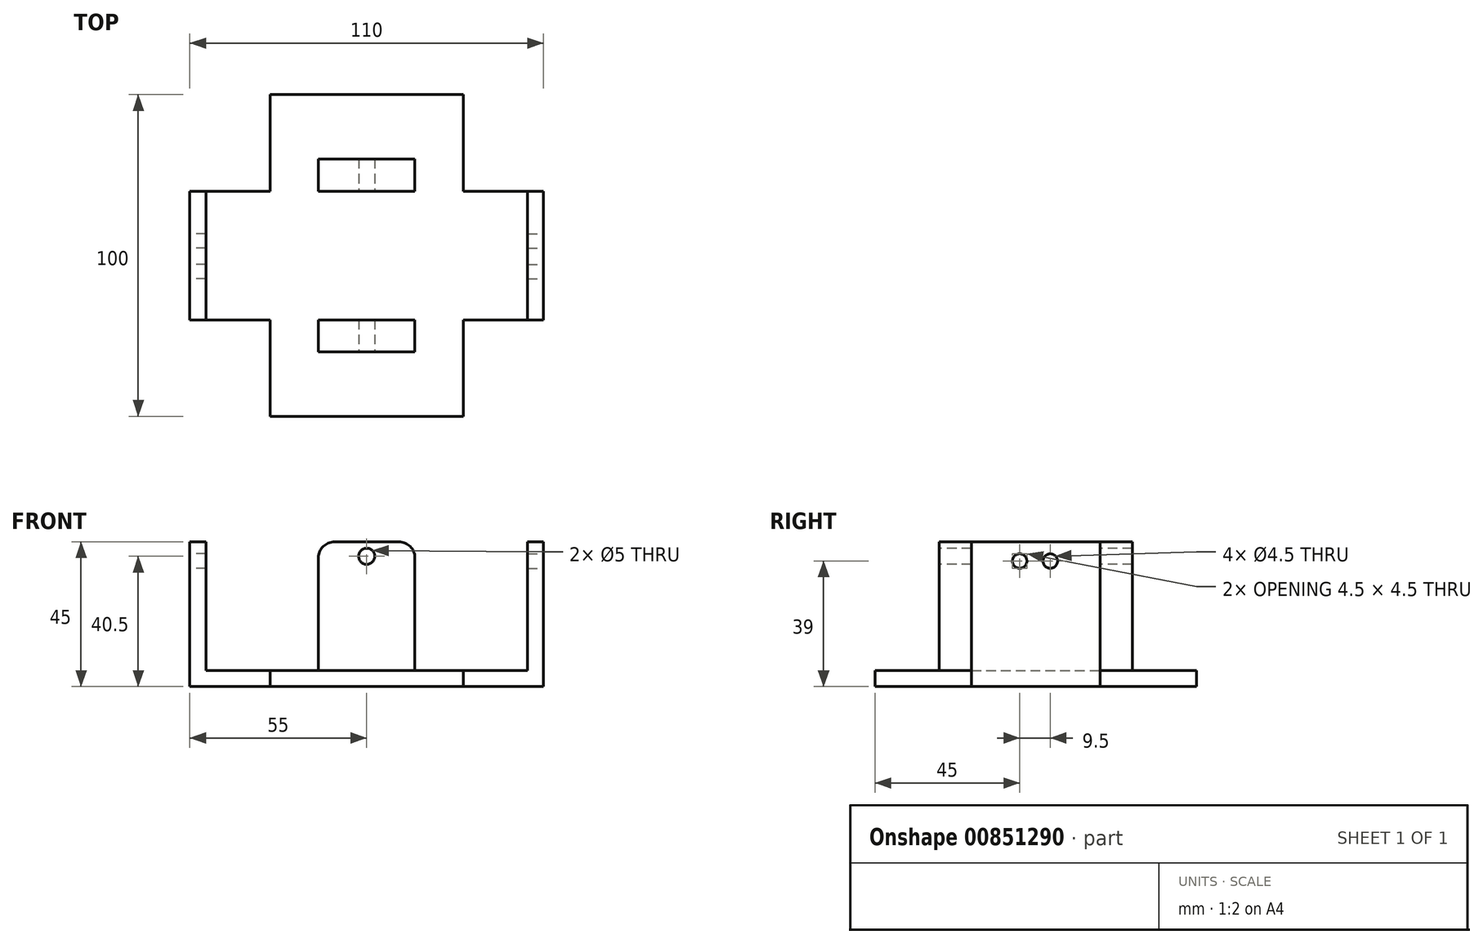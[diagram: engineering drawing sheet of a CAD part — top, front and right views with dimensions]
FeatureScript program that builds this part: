
annotation { "Feature Type Name" : "Feature", "Feature Type Description" : "" }
export const myFeature = defineFeature(function(context is Context, id is Id, definition is map)
    precondition{}
    {
        {
            var Q0;
            Q0=qCreatedBy(makeId("Top.planeOp"),FACE);
            var sketch = newSketch(context, id + "F0", { "sketchPlane" : qUnion([Q0])});
            skLineSegment(sketch, "E0.bottom", {"start": v(-30, -50) * mm, "end": v(30, -50) * mm});
            skLineSegment(sketch, "E0.top", {"start": v(-30, 50) * mm, "end": v(30, 50) * mm});
            skLineSegment(sketch, "E0.left", {"start": v(-30, -50) * mm, "end": v(-30, 50) * mm});
            skLineSegment(sketch, "E0.right", {"start": v(30, -50) * mm, "end": v(30, 50) * mm});
            skLineSegment(sketch, "E1", {"start": v(0, 50) * mm, "end": v(0, -50) * mm});
            skSolve(sketch);
        }
        {
            var Q0;
            {var subQ0=sQuery(id+"F0.wireOp",EDGE,"E0.left");Q0=makeQuery(id+"F0.imprint","IMPRINT",FACE,{"disambiguationData":[TD([[makeQuery(id+"F0.imprint","IMPRINT",EDGE,{"derivedFrom":subQ0}),-1.0]])]});}
            var Q1;
            {var subQ0=sQuery(id+"F0.wireOp",EDGE,"E0.right");Q1=makeQuery(id+"F0.imprint","IMPRINT",FACE,{"disambiguationData":[TD([[makeQuery(id+"F0.imprint","IMPRINT",EDGE,{"derivedFrom":subQ0}),1.0]])]});}
            extrude(context, id + "F1", {"entities" : qUnion([Q0, Q1]), "depth" : 5 * mm, "offsetDistance" : 25 * mm});
        }
        {
            var Q0;
            Q0=makeQuery(id+"F1.opExtrude","CAP_FACE",FACE,{"disambiguationData":[OSD([sQuery(id+"F0.wireOp",EDGE,"E0.bottom"),sQuery(id+"F0.wireOp",EDGE,"E0.top"),sQuery(id+"F0.wireOp",EDGE,"E0.left"),sQuery(id+"F0.wireOp",EDGE,"E0.right")])],"isStart":false});
            var sketch = newSketch(context, id + "F2", { "sketchPlane" : qUnion([Q0])});
            skLineSegment(sketch, "E2.bottom", {"start": v(-15, -20) * mm, "end": v(15, -20) * mm});
            skLineSegment(sketch, "E2.top", {"start": v(-15, -30) * mm, "end": v(15, -30) * mm});
            skLineSegment(sketch, "E2.left", {"start": v(-15, -20) * mm, "end": v(-15, -30) * mm});
            skLineSegment(sketch, "E2.right", {"start": v(15, -20) * mm, "end": v(15, -30) * mm});
            skLineSegment(sketch, "E3", {"start": v(-30, 0) * mm, "end": v(30, 0) * mm});
            skLineSegment(sketch, "E4.MirrorCS", {"start": v(-15, 20) * mm, "end": v(15, 20) * mm});
            skLineSegment(sketch, "E5.MirrorCS", {"start": v(15, 20) * mm, "end": v(15, 30) * mm});
            skLineSegment(sketch, "E6.MirrorCS", {"start": v(-15, 30) * mm, "end": v(15, 30) * mm});
            skLineSegment(sketch, "E7.MirrorCS", {"start": v(-15, 20) * mm, "end": v(-15, 30) * mm});
            skSolve(sketch);
        }
        {
            var Q0;
            Q0=makeQuery(id+"F2.imprint","IMPRINT",FACE,{"disambiguationData":[TD([[makeQuery(id+"F2.imprint","IMPRINT",EDGE,{"derivedFrom":sQuery(id+"F2.wireOp",EDGE,"E4.MirrorCS")}),1.0]])]});
            var Q1;
            Q1=makeQuery(id+"F2.imprint","IMPRINT",FACE,{"disambiguationData":[TD([[makeQuery(id+"F2.imprint","IMPRINT",EDGE,{"derivedFrom":sQuery(id+"F2.wireOp",EDGE,"E2.bottom")}),-1.0]])]});
            extrude(context, id + "F3", {"entities" : qUnion([Q0, Q1]), "operationType" : NewBodyOperationType.ADD, "depth" : 40 * mm, "offsetDistance" : 25 * mm});
        }
        {
            var Q0;
            Q0=makeQuery(id+"F3.opExtrude","CAP_EDGE",EDGE,{"disambiguationData":[OSD([sQuery(id+"F2.wireOp",EDGE,"E2.left")])],"isStart":false});
            var Q1;
            Q1=makeQuery(id+"F3.opExtrude","CAP_EDGE",EDGE,{"disambiguationData":[OSD([sQuery(id+"F2.wireOp",EDGE,"E2.right")])],"isStart":false});
            var Q2;
            Q2=makeQuery(id+"F3.opExtrude","CAP_EDGE",EDGE,{"disambiguationData":[OSD([sQuery(id+"F2.wireOp",EDGE,"E7.MirrorCS")])],"isStart":false});
            var Q3;
            Q3=makeQuery(id+"F3.opExtrude","CAP_EDGE",EDGE,{"disambiguationData":[OSD([sQuery(id+"F2.wireOp",EDGE,"E5.MirrorCS")])],"isStart":false});
            fillet(context, id + "F4", {"entities" : qUnion([Q0, Q1, Q2, Q3]), "radius" : 5 * mm, "tangentPropagation" : true, "allowEdgeOverflow" : false});
        }
        {
            var Q0;
            Q0=makeQuery(id+"F3.opExtrude","SWEPT_FACE",FACE,{"disambiguationData":[OSD([sQuery(id+"F2.wireOp",EDGE,"E2.top")])]});
            var sketch = newSketch(context, id + "F5", { "sketchPlane" : qUnion([Q0])});
            skCircle(sketch, "E8", {"center": v(0, 40.5) * mm, "radius": 2.5 * mm});
            skSolve(sketch);
        }
        {
            var Q0;
            Q0=makeQuery(id+"F5.imprint","IMPRINT",FACE,{"disambiguationData":[TD([[makeQuery(id+"F5.imprint","IMPRINT",EDGE,{"derivedFrom":sQuery(id+"F5.wireOp",EDGE,"E8")}),1.0]])]});
            extrude(context, id + "F6", {"entities" : qUnion([Q0]), "operationType" : NewBodyOperationType.REMOVE, "endBound" : BoundingType.THROUGH_ALL, "oppositeDirection" : true, "depth" : 25 * mm, "offsetDistance" : 25 * mm});
        }
        {
            var Q0;
            Q0=makeQuery(id+"F1.opExtrude","SWEPT_FACE",FACE,{"disambiguationData":[OSD([sQuery(id+"F0.wireOp",EDGE,"E0.right")])]});
            var sketch = newSketch(context, id + "F7", { "sketchPlane" : qUnion([Q0])});
            skLineSegment(sketch, "E9.bottom", {"start": v(-20, 5) * mm, "end": v(20, 5) * mm});
            skLineSegment(sketch, "E9.top", {"start": v(-20, 0) * mm, "end": v(20, 0) * mm});
            skLineSegment(sketch, "E9.left", {"start": v(-20, 5) * mm, "end": v(-20, 0) * mm});
            skLineSegment(sketch, "E9.right", {"start": v(20, 5) * mm, "end": v(20, 0) * mm});
            skSolve(sketch);
        }
        {
            var Q0;
            Q0=makeQuery(id+"F7.imprint","IMPRINT",FACE,{"disambiguationData":[TD([[makeQuery(id+"F7.imprint","IMPRINT",EDGE,{"derivedFrom":sQuery(id+"F7.wireOp",EDGE,"E9.bottom")}),-1.0]])]});
            extrude(context, id + "F8", {"entities" : qUnion([Q0]), "operationType" : NewBodyOperationType.ADD, "depth" : 25 * mm, "offsetDistance" : 25 * mm});
        }
        {
            var Q0;
            Q0=makeQuery(id+"F8.boolean.opBoolean","MERGE",FACE,{"derivedFrom":[makeQuery(id+"F1.opExtrude","CAP_FACE",FACE,{"disambiguationData":[OSD([sQuery(id+"F0.wireOp",EDGE,"E0.bottom"),sQuery(id+"F0.wireOp",EDGE,"E0.top"),sQuery(id+"F0.wireOp",EDGE,"E0.left"),sQuery(id+"F0.wireOp",EDGE,"E0.right")])],"isStart":false}),makeQuery(id+"F8.opExtrude","SWEPT_FACE",FACE,{"disambiguationData":[OSD([sQuery(id+"F7.wireOp",EDGE,"E9.bottom")])]})]});
            var sketch = newSketch(context, id + "F9", { "sketchPlane" : qUnion([Q0])});
            skLineSegment(sketch, "E10.bottom", {"start": v(55, -20) * mm, "end": v(50, -20) * mm});
            skLineSegment(sketch, "E10.top", {"start": v(55, 20) * mm, "end": v(50, 20) * mm});
            skLineSegment(sketch, "E10.left", {"start": v(55, -20) * mm, "end": v(55, 20) * mm});
            skLineSegment(sketch, "E10.right", {"start": v(50, -20) * mm, "end": v(50, 20) * mm});
            skSolve(sketch);
        }
        {
            var Q0;
            Q0=makeQuery(id+"F9.imprint","IMPRINT",FACE,{"disambiguationData":[TD([[makeQuery(id+"F9.imprint","IMPRINT",EDGE,{"derivedFrom":sQuery(id+"F9.wireOp",EDGE,"E10.bottom")}),-1.0]])]});
            extrude(context, id + "F10", {"entities" : qUnion([Q0]), "operationType" : NewBodyOperationType.ADD, "depth" : 40 * mm, "offsetDistance" : 25 * mm});
        }
        {
            var Q0;
            Q0=makeQuery(id+"F10.boolean.opBoolean","MERGE",FACE,{"derivedFrom":[makeQuery(id+"F8.opExtrude","CAP_FACE",FACE,{"disambiguationData":[OSD([sQuery(id+"F7.wireOp",EDGE,"E9.bottom"),sQuery(id+"F7.wireOp",EDGE,"E9.top"),sQuery(id+"F7.wireOp",EDGE,"E9.left"),sQuery(id+"F7.wireOp",EDGE,"E9.right")])],"isStart":false}),makeQuery(id+"F10.opExtrude","SWEPT_FACE",FACE,{"disambiguationData":[OSD([sQuery(id+"F9.wireOp",EDGE,"E10.left")])]})]});
            var sketch = newSketch(context, id + "F11", { "sketchPlane" : qUnion([Q0])});
            skCircle(sketch, "E11", {"center": v(-5, 39) * mm, "radius": 2.25 * mm});
            skCircle(sketch, "E12", {"center": v(4.5, 39) * mm, "radius": 2.25 * mm});
            skSolve(sketch);
        }
        {
            var Q0;
            Q0=makeQuery(id+"F11.imprint","IMPRINT",FACE,{"disambiguationData":[TD([[makeQuery(id+"F11.imprint","IMPRINT",EDGE,{"derivedFrom":sQuery(id+"F11.wireOp",EDGE,"E11")}),1.0]])]});
            var Q1;
            Q1=makeQuery(id+"F11.imprint","IMPRINT",FACE,{"disambiguationData":[TD([[makeQuery(id+"F11.imprint","IMPRINT",EDGE,{"derivedFrom":sQuery(id+"F11.wireOp",EDGE,"E12")}),1.0]])]});
            extrude(context, id + "F12", {"entities" : qUnion([Q0, Q1]), "operationType" : NewBodyOperationType.REMOVE, "oppositeDirection" : true, "depth" : 25 * mm, "offsetDistance" : 25 * mm});
        }
        {
            var Q0;
            Q0=makeQuery(id+"F8.boolean.opBoolean","MERGE",FACE,{"derivedFrom":[makeQuery(id+"F1.opExtrude","CAP_FACE",FACE,{"disambiguationData":[OSD([sQuery(id+"F0.wireOp",EDGE,"E0.bottom"),sQuery(id+"F0.wireOp",EDGE,"E0.top"),sQuery(id+"F0.wireOp",EDGE,"E0.left"),sQuery(id+"F0.wireOp",EDGE,"E0.right")])],"isStart":false}),makeQuery(id+"F8.opExtrude","SWEPT_FACE",FACE,{"disambiguationData":[OSD([sQuery(id+"F7.wireOp",EDGE,"E9.bottom")])]})]});
            var sketch = newSketch(context, id + "F13", { "sketchPlane" : qUnion([Q0])});
            skLineSegment(sketch, "E13", {"start": v(0, 20) * mm, "end": v(0, -20) * mm});
            skSolve(sketch);
        }
        {
            var Q0;
            Q0 = qSketchRegion(id + "F13", true);
            var Q1;
            Q1 = qConstructionFilter(qBodyType(qCreatedBy(id + "F13" ,EDGE), BodyType.WIRE), ConstructionObject.NO);
            extrude(context, id + "F14", {"entities" : qUnion([Q0]), "bodyType" : ToolBodyType.SURFACE, "surfaceEntities" : qUnion([Q1]), "depth" : 1 * mm, "offsetDistance" : 25 * mm});
        }
        {
            var Q0;
            Q0=makeQuery(id+"F1.opExtrude","SWEPT_BODY",BODY,{"disambiguationData":[OSD([sQuery(id+"F0.wireOp",EDGE,"E0.bottom"),sQuery(id+"F0.wireOp",EDGE,"E0.top"),sQuery(id+"F0.wireOp",EDGE,"E0.left"),sQuery(id+"F0.wireOp",EDGE,"E0.right")])]});
            var Q1;
            Q1=makeQuery(id+"F14.opExtrude","SWEPT_FACE",FACE,{"disambiguationData":[OSD([sQuery(id+"F13.wireOp",EDGE,"E13")])]});
            mirror(context, id + "F15", {"operationType" : NewBodyOperationType.ADD, "entities" : qUnion([Q0]), "mirrorPlane" : qUnion([Q1])});
        }
    });
